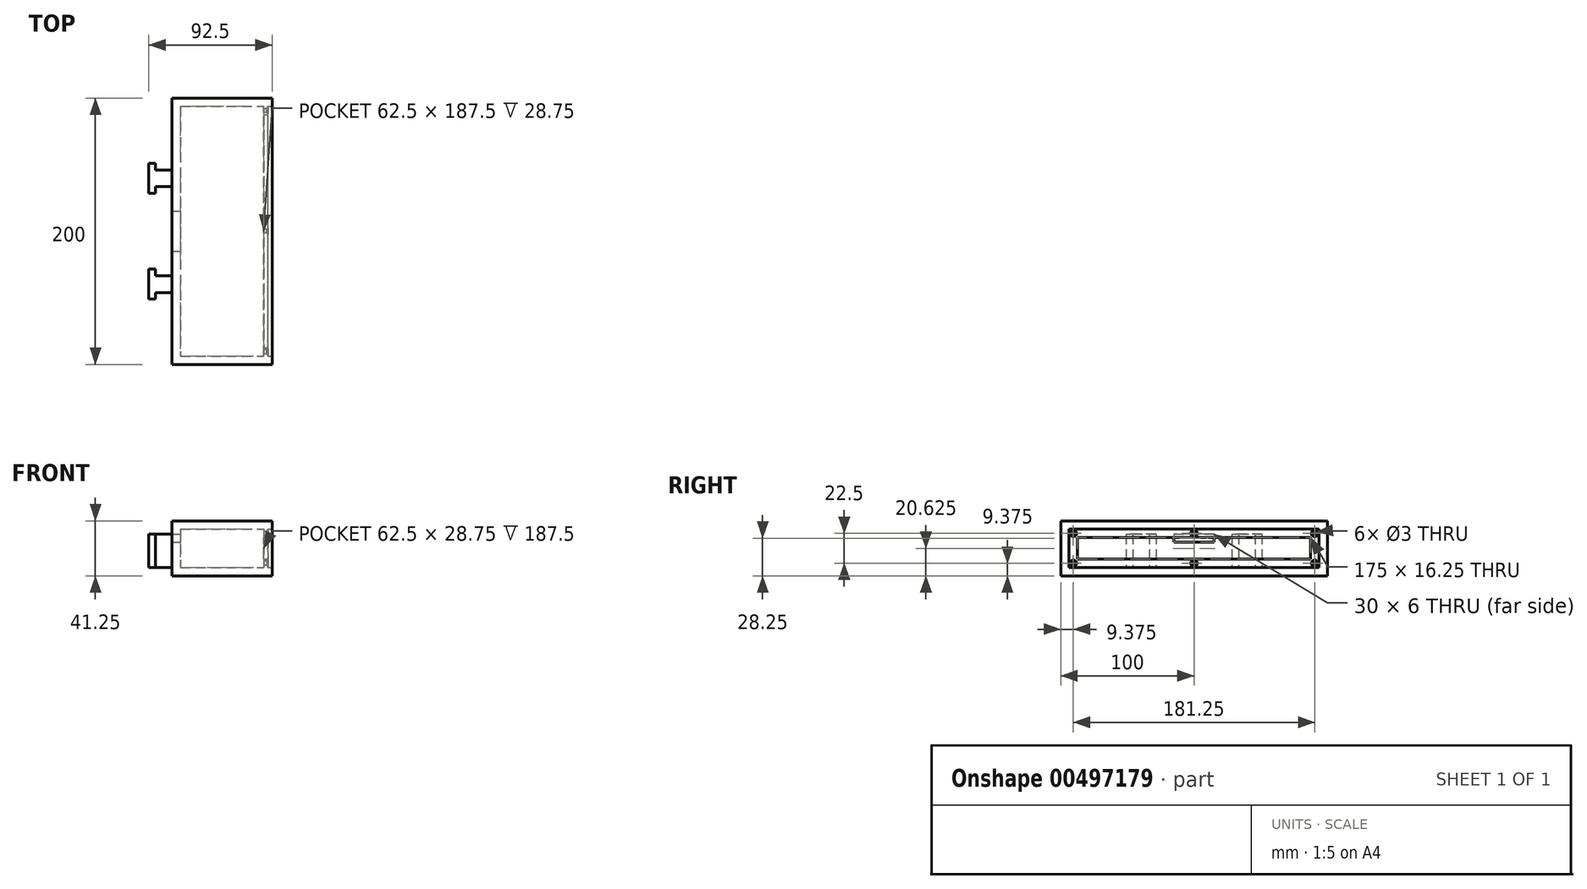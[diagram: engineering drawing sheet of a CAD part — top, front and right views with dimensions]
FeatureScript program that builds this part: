
annotation { "Feature Type Name" : "Feature", "Feature Type Description" : "" }
export const myFeature = defineFeature(function(context is Context, id is Id, definition is map)
    precondition{}
    {
        {
            var Q0;
            Q0=qCreatedBy(makeId("Top.planeOp"),FACE);
            var sketch = newSketch(context, id + "F0", { "sketchPlane" : qUnion([Q0])});
            skPoint(sketch, "E0", {"position": v(0, 100) * mm});
            skPoint(sketch, "E1", {"position": v(0, -100) * mm});
            skLineSegment(sketch, "E2", {"start": v(0, 100) * mm, "end": v(0, -100) * mm});
            skLineSegment(sketch, "E3", {"start": v(0, 100) * mm, "end": v(-75, 100) * mm});
            skLineSegment(sketch, "E4", {"start": v(0, -100) * mm, "end": v(-75, -100) * mm});
            skLineSegment(sketch, "E5", {"start": v(-75, -100) * mm, "end": v(-75, 100) * mm});
            skPoint(sketch, "E6", {"position": v(-68.75, 93.75) * mm});
            skPoint(sketch, "E7", {"position": v(-6.25, 93.75) * mm});
            skPoint(sketch, "E8", {"position": v(-6.25, -93.75) * mm});
            skPoint(sketch, "E9", {"position": v(-68.75, -93.75) * mm});
            skLineSegment(sketch, "E10", {"start": v(-68.75, 93.75) * mm, "end": v(-6.25, 93.75) * mm});
            skLineSegment(sketch, "E11", {"start": v(-6.25, -93.75) * mm, "end": v(-6.25, 93.75) * mm});
            skLineSegment(sketch, "E12", {"start": v(-68.75, -93.75) * mm, "end": v(-6.25, -93.75) * mm});
            skLineSegment(sketch, "E13", {"start": v(-68.75, 93.75) * mm, "end": v(-68.75, -93.75) * mm});
            skPoint(sketch, "E14", {"position": v(-75, 15) * mm});
            skPoint(sketch, "E15", {"position": v(-75, -15) * mm});
            skPoint(sketch, "E16", {"position": v(-75, 46) * mm});
            skPoint(sketch, "E17", {"position": v(-75, 33.5) * mm});
            skPoint(sketch, "E18", {"position": v(-75, -33.5) * mm});
            skPoint(sketch, "E19", {"position": v(-75, -46) * mm});
            skLineSegment(sketch, "E20", {"start": v(-75, 46) * mm, "end": v(-87.5, 46) * mm});
            skLineSegment(sketch, "E21", {"start": v(-87.5, 46) * mm, "end": v(-87.5, 51) * mm});
            skLineSegment(sketch, "E22", {"start": v(-87.5, 51) * mm, "end": v(-92.5, 51) * mm});
            skLineSegment(sketch, "E23", {"start": v(-92.5, 51) * mm, "end": v(-92.5, 28.5) * mm});
            skLineSegment(sketch, "E24", {"start": v(-92.5, 28.5) * mm, "end": v(-87.5, 28.5) * mm});
            skLineSegment(sketch, "E25", {"start": v(-87.5, 28.5) * mm, "end": v(-87.5, 33.5) * mm});
            skLineSegment(sketch, "E26", {"start": v(-87.5, 33.5) * mm, "end": v(-75, 33.5) * mm});
            skLineSegment(sketch, "E27", {"start": v(-75, -33.5) * mm, "end": v(-87.5, -33.5) * mm});
            skLineSegment(sketch, "E28", {"start": v(-87.5, -33.5) * mm, "end": v(-87.5, -28.5) * mm});
            skLineSegment(sketch, "E29", {"start": v(-87.5, -28.5) * mm, "end": v(-92.5, -28.5) * mm});
            skLineSegment(sketch, "E30", {"start": v(-92.5, -28.5) * mm, "end": v(-92.5, -51) * mm});
            skLineSegment(sketch, "E31", {"start": v(-92.5, -51) * mm, "end": v(-87.5, -51) * mm});
            skLineSegment(sketch, "E32", {"start": v(-87.5, -51) * mm, "end": v(-87.5, -46) * mm});
            skLineSegment(sketch, "E33", {"start": v(-87.5, -46) * mm, "end": v(-75, -46) * mm});
            skPoint(sketch, "E34", {"position": v(-68.75, 15) * mm});
            skPoint(sketch, "E35", {"position": v(-68.75, -15) * mm});
            skLineSegment(sketch, "E36", {"start": v(-75, 15) * mm, "end": v(-68.75, 15) * mm});
            skLineSegment(sketch, "E37", {"start": v(-75, -15) * mm, "end": v(-68.75, -15) * mm});
            skSolve(sketch);
        }
        {
            var Q0;
            Q0=makeQuery(id+"F0.imprint","IMPRINT",FACE,{"disambiguationData":[TD([[makeQuery(id+"F0.imprint","IMPRINT",EDGE,{"derivedFrom":sQuery(id+"F0.wireOp",EDGE,"E2")}),-1.0]])]});
            extrude(context, id + "F1", {"entities" : qUnion([Q0]), "depth" : 41.25 * mm});
        }
        {
            var Q0;
            {var subQ0=sQuery(id+"F0.wireOp",EDGE,"E36");Q0=makeQuery(id+"F0.imprint","IMPRINT",FACE,{"disambiguationData":[TD([[makeQuery(id+"F0.imprint","IMPRINT",EDGE,{"derivedFrom":subQ0}),-1.0]])]});}
            extrude(context, id + "F2", {"entities" : qUnion([Q0]), "operationType" : NewBodyOperationType.ADD, "depth" : 25.25 * mm});
        }
        {
            var Q0;
            Q0=makeQuery(id+"F2.opExtrude","CAP_FACE",FACE,{"disambiguationData":[OSD([sQuery(id+"F0.wireOp",EDGE,"E5"),sQuery(id+"F0.wireOp",EDGE,"E13"),sQuery(id+"F0.wireOp",EDGE,"E36"),sQuery(id+"F0.wireOp",EDGE,"E37")])],"isStart":false});
            extrude(context, id + "F3", {"entities" : qUnion([Q0]), "operationType" : NewBodyOperationType.ADD, "depth" : 16 * mm, "hasSecondDirection" : true, "secondDirectionOppositeDirection" : false, "secondDirectionDepth" : 6 * mm});
        }
        {
            var Q0;
            {var subQ0=sQuery(id+"F0.wireOp",EDGE,"E20");Q0=makeQuery(id+"F0.imprint","IMPRINT",FACE,{"disambiguationData":[TD([[makeQuery(id+"F0.imprint","IMPRINT",EDGE,{"derivedFrom":subQ0}),1.0]])]});}
            var Q1;
            {var subQ0=sQuery(id+"F0.wireOp",EDGE,"E27");Q1=makeQuery(id+"F0.imprint","IMPRINT",FACE,{"disambiguationData":[TD([[makeQuery(id+"F0.imprint","IMPRINT",EDGE,{"derivedFrom":subQ0}),1.0]])]});}
            extrude(context, id + "F4", {"entities" : qUnion([Q0, Q1]), "operationType" : NewBodyOperationType.ADD, "depth" : 31.25 * mm, "hasSecondDirection" : true, "secondDirectionOppositeDirection" : false, "secondDirectionDepth" : 6.25 * mm});
        }
        {
            var Q0;
            {var subQ1=sQuery(id+"F0.wireOp",EDGE,"E10");Q0=makeQuery(id+"F0.imprint","IMPRINT",FACE,{"disambiguationData":[TD([[makeQuery(id+"F0.imprint","IMPRINT",EDGE,{"derivedFrom":subQ1}),-1.0]])]});}
            extrude(context, id + "F5", {"entities" : qUnion([Q0]), "operationType" : NewBodyOperationType.ADD, "depth" : 41.25 * mm, "hasSecondDirection" : true, "secondDirectionOppositeDirection" : false, "secondDirectionDepth" : 35 * mm});
        }
        {
            var Q0;
            {var subQ1=sQuery(id+"F0.wireOp",EDGE,"E10");Q0=makeQuery(id+"F0.imprint","IMPRINT",FACE,{"disambiguationData":[TD([[makeQuery(id+"F0.imprint","IMPRINT",EDGE,{"derivedFrom":subQ1}),-1.0]])]});}
            extrude(context, id + "F6", {"entities" : qUnion([Q0]), "operationType" : NewBodyOperationType.ADD, "depth" : 6.25 * mm});
        }
        {
            var Q0;
            Q0=makeQuery(id+"F1.opExtrude","SWEPT_FACE",FACE,{"disambiguationData":[OSD([sQuery(id+"F0.wireOp",EDGE,"E2")])]});
            var sketch = newSketch(context, id + "F7", { "sketchPlane" : qUnion([Q0])});
            skPoint(sketch, "E38", {"position": v(-93.75, 41.25) * mm});
            skPoint(sketch, "E39", {"position": v(-93.75, 0) * mm});
            skPoint(sketch, "E40", {"position": v(93.75, 41.25) * mm});
            skPoint(sketch, "E41", {"position": v(93.75, 0) * mm});
            skPoint(sketch, "E42", {"position": v(-100, 35) * mm});
            skPoint(sketch, "E43", {"position": v(100, 35) * mm});
            skPoint(sketch, "E44", {"position": v(100, 6.25) * mm});
            skPoint(sketch, "E45", {"position": v(-100, 6.25) * mm});
            skPoint(sketch, "E46", {"position": v(-93.75, 35) * mm});
            skPoint(sketch, "E47", {"position": v(-93.75, 6.25) * mm});
            skPoint(sketch, "E48", {"position": v(93.75, 35) * mm});
            skPoint(sketch, "E49", {"position": v(93.75, 6.25) * mm});
            skLineSegment(sketch, "E50", {"start": v(-93.75, 35) * mm, "end": v(93.75, 35) * mm});
            skLineSegment(sketch, "E51", {"start": v(93.75, 6.25) * mm, "end": v(93.75, 35) * mm});
            skLineSegment(sketch, "E52", {"start": v(93.75, 6.25) * mm, "end": v(-93.75, 6.25) * mm});
            skLineSegment(sketch, "E53", {"start": v(-93.75, 6.25) * mm, "end": v(-93.75, 35) * mm});
            skPoint(sketch, "E54", {"position": v(-87.5, 35) * mm});
            skPoint(sketch, "E55", {"position": v(-87.5, 6.25) * mm});
            skPoint(sketch, "E56", {"position": v(87.5, 35) * mm});
            skPoint(sketch, "E57", {"position": v(87.5, 6.25) * mm});
            skPoint(sketch, "E58", {"position": v(-93.75, 28.75) * mm});
            skPoint(sketch, "E59", {"position": v(93.75, 28.75) * mm});
            skPoint(sketch, "E60", {"position": v(93.75, 12.5) * mm});
            skPoint(sketch, "E61", {"position": v(-93.75, 12.5) * mm});
            skPoint(sketch, "E62", {"position": v(-87.5, 28.75) * mm});
            skPoint(sketch, "E63", {"position": v(-87.5, 12.5) * mm});
            skPoint(sketch, "E64", {"position": v(87.5, 28.75) * mm});
            skPoint(sketch, "E65", {"position": v(87.5, 12.5) * mm});
            skLineSegment(sketch, "E66", {"start": v(87.5, 28.75) * mm, "end": v(87.5, 12.5) * mm});
            skLineSegment(sketch, "E67", {"start": v(87.5, 12.5) * mm, "end": v(-87.5, 12.5) * mm});
            skLineSegment(sketch, "E68", {"start": v(-87.5, 12.5) * mm, "end": v(-87.5, 28.75) * mm});
            skLineSegment(sketch, "E69", {"start": v(-87.5, 28.75) * mm, "end": v(87.5, 28.75) * mm});
            skPoint(sketch, "E70", {"position": v(-90.62, 31.87) * mm});
            skPoint(sketch, "E71", {"position": v(90.63, 31.88) * mm});
            skPoint(sketch, "E72", {"position": v(90.63, 9.37) * mm});
            skPoint(sketch, "E73", {"position": v(-90.62, 9.37) * mm});
            skPoint(sketch, "E74", {"position": v(0, 31.87) * mm});
            skPoint(sketch, "E74.positionSnap0", {"position": v(0, 35) * mm});
            skPoint(sketch, "E75", {"position": v(0, 9.37) * mm});
            skPoint(sketch, "E75.positionSnap0", {"position": v(0, 6.25) * mm});
            skSolve(sketch);
        }
        {
            var Q0;
            Q0=makeQuery(id+"F7.imprint","IMPRINT",FACE,{"disambiguationData":[TD([[makeQuery(id+"F7.imprint","IMPRINT",EDGE,{"derivedFrom":sQuery(id+"F7.wireOp",EDGE,"E66")}),-1.0]])]});
            extrude(context, id + "F8", {"entities" : qUnion([Q0]), "operationType" : NewBodyOperationType.REMOVE, "oppositeDirection" : true, "depth" : 10 * mm});
        }
        {
            var Q0;
            Q0=makeQuery(id+"F7.imprint","IMPRINT",FACE,{"disambiguationData":[TD([[makeQuery(id+"F7.imprint","IMPRINT",EDGE,{"derivedFrom":sQuery(id+"F7.wireOp",EDGE,"E50")}),-1.0]])]});
            extrude(context, id + "F9", {"entities" : qUnion([Q0]), "operationType" : NewBodyOperationType.REMOVE, "oppositeDirection" : true, "depth" : 3 * mm});
        }
        {
            var Q0;
            Q0=makeQuery(id+"F9.boolean.opBoolean","COPY",FACE,{"derivedFrom":makeQuery(id+"F9.opExtrude","CAP_FACE",FACE,{"disambiguationData":[OSD([sQuery(id+"F7.wireOp",EDGE,"E50"),sQuery(id+"F7.wireOp",EDGE,"E51"),sQuery(id+"F7.wireOp",EDGE,"E52"),sQuery(id+"F7.wireOp",EDGE,"E53"),sQuery(id+"F7.wireOp",EDGE,"E66"),sQuery(id+"F7.wireOp",EDGE,"E67"),sQuery(id+"F7.wireOp",EDGE,"E68"),sQuery(id+"F7.wireOp",EDGE,"E69")])],"isStart":false})});
            var sketch = newSketch(context, id + "F10", { "sketchPlane" : qUnion([Q0])});
            skPoint(sketch, "E76", {"position": v(-90.62, 31.87) * mm});
            skPoint(sketch, "E77", {"position": v(-90.62, 9.37) * mm});
            skPoint(sketch, "E78", {"position": v(90.63, 9.37) * mm});
            skPoint(sketch, "E79", {"position": v(90.62, 31.88) * mm});
            skPoint(sketch, "E80", {"position": v(0, 31.88) * mm});
            skPoint(sketch, "E81", {"position": v(0, 9.37) * mm});
            skSolve(sketch);
        }
        {
            var Q0;
            Q0=sQuery(id+"F10.wireOp",VERTEX,"E76");
            var Q1;
            Q1=sQuery(id+"F10.wireOp",VERTEX,"E80");
            var Q2;
            Q2=sQuery(id+"F10.wireOp",VERTEX,"E79");
            var Q3;
            Q3=sQuery(id+"F10.wireOp",VERTEX,"E78");
            var Q4;
            Q4=sQuery(id+"F10.wireOp",VERTEX,"E81");
            var Q5;
            Q5=sQuery(id+"F10.wireOp",VERTEX,"E77");
            var Q6;
            Q6=makeQuery(id+"F1.opExtrude","SWEPT_BODY",BODY,{"disambiguationData":[OSD([sQuery(id+"F0.wireOp",EDGE,"E2"),sQuery(id+"F0.wireOp",EDGE,"E3"),sQuery(id+"F0.wireOp",EDGE,"E4"),sQuery(id+"F0.wireOp",EDGE,"E5"),sQuery(id+"F0.wireOp",EDGE,"E10"),sQuery(id+"F0.wireOp",EDGE,"E11"),sQuery(id+"F0.wireOp",EDGE,"E12"),sQuery(id+"F0.wireOp",EDGE,"E13"),sQuery(id+"F0.wireOp",EDGE,"E36"),sQuery(id+"F0.wireOp",EDGE,"E37")])]});
            hole(context, id + "F11", {"style" : HoleStyle.C_SINK, "endStyle" : HoleEndStyle.BLIND, "holeDiameter" : 3 * mm, "cSinkDiameter" : 5 * mm, "cSinkAngle" : 90 * degree, "holeDepth" : 12 * mm, "isTappedThrough" : true, "tappedDepth" : 12 * mm, "tapClearance" : 3, "locations" : qUnion([Q0, Q1, Q2, Q3, Q4, Q5]), "scope" : qUnion([Q6])});
        }
    });
